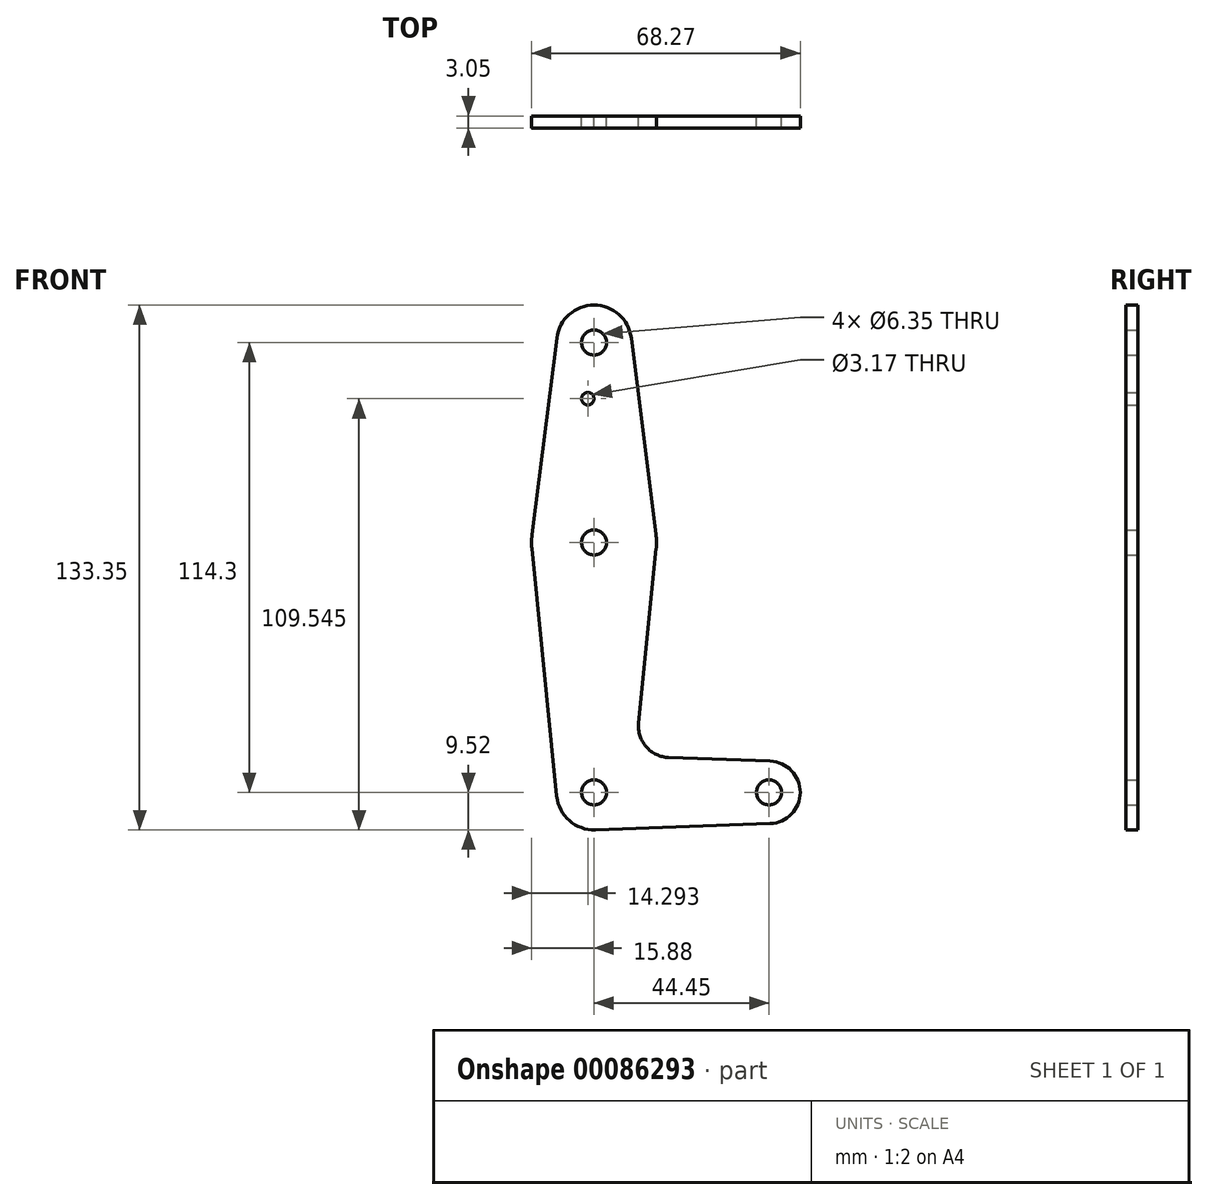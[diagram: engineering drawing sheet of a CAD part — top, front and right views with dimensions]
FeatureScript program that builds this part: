
annotation { "Feature Type Name" : "Feature", "Feature Type Description" : "" }
export const myFeature = defineFeature(function(context is Context, id is Id, definition is map)
    precondition{}
    {
        {
            var Q0;
            Q0=qCreatedBy(makeId("Front.planeOp"),FACE);
            var sketch = newSketch(context, id + "F0", { "sketchPlane" : qUnion([Q0])});
            skLineSegment(sketch, "E0", {"start": v(0, 114.3) * mm, "end": v(0, 0) * mm, "construction": true});
            skLineSegment(sketch, "E1", {"start": v(0, 0) * mm, "end": v(44.45, 0) * mm, "construction": true});
            skCircle(sketch, "E2", {"center": v(0, 114.3) * mm, "radius": 9.53 * mm});
            skCircle(sketch, "E3", {"center": v(0, 63.5) * mm, "radius": 15.88 * mm});
            skCircle(sketch, "E4", {"center": v(0, 0) * mm, "radius": 9.53 * mm});
            skCircle(sketch, "E5", {"center": v(44.45, 0) * mm, "radius": 7.94 * mm});
            skLineSegment(sketch, "E6", {"start": v(9.45, 115.5) * mm, "end": v(15.75, 65.48) * mm});
            skLineSegment(sketch, "E7", {"start": v(-9.45, 115.5) * mm, "end": v(-15.75, 65.48) * mm});
            skLineSegment(sketch, "E8", {"start": v(-15.8, 61.91) * mm, "end": v(-9.48, -0.95) * mm});
            skLineSegment(sketch, "E9", {"start": v(15.8, 61.91) * mm, "end": v(11.34, 17.6) * mm});
            skLineSegment(sketch, "E10", {"start": v(0.34, -9.52) * mm, "end": v(44.73, -7.93) * mm});
            skLineSegment(sketch, "E11", {"start": v(18.97, 8.85) * mm, "end": v(44.73, 7.93) * mm});
            skCircle(sketch, "E12", {"center": v(0, 114.3) * mm, "radius": 3.18 * mm});
            skCircle(sketch, "E13", {"center": v(0, 63.5) * mm, "radius": 3.18 * mm});
            skCircle(sketch, "E14", {"center": v(0, 0) * mm, "radius": 3.18 * mm});
            skCircle(sketch, "E15", {"center": v(44.45, 0) * mm, "radius": 3.18 * mm});
            skCircle(sketch, "E16", {"center": v(-1.59, 100.03) * mm, "radius": 1.59 * mm});
            skArc(sketch, "E17.filletArc", {"start": v(11.34, 17.6) * mm, "mid": v(13.26, 11.57) * mm, "end": v(18.97, 8.85) * mm});
            skSolve(sketch);
        }
        {
            var Q0;
            Q0 = qSketchRegion(id + "F0", true);
            extrude(context, id + "F1", {"entities" : qUnion([Q0]), "depth" : 3.05 * mm});
        }
    });
